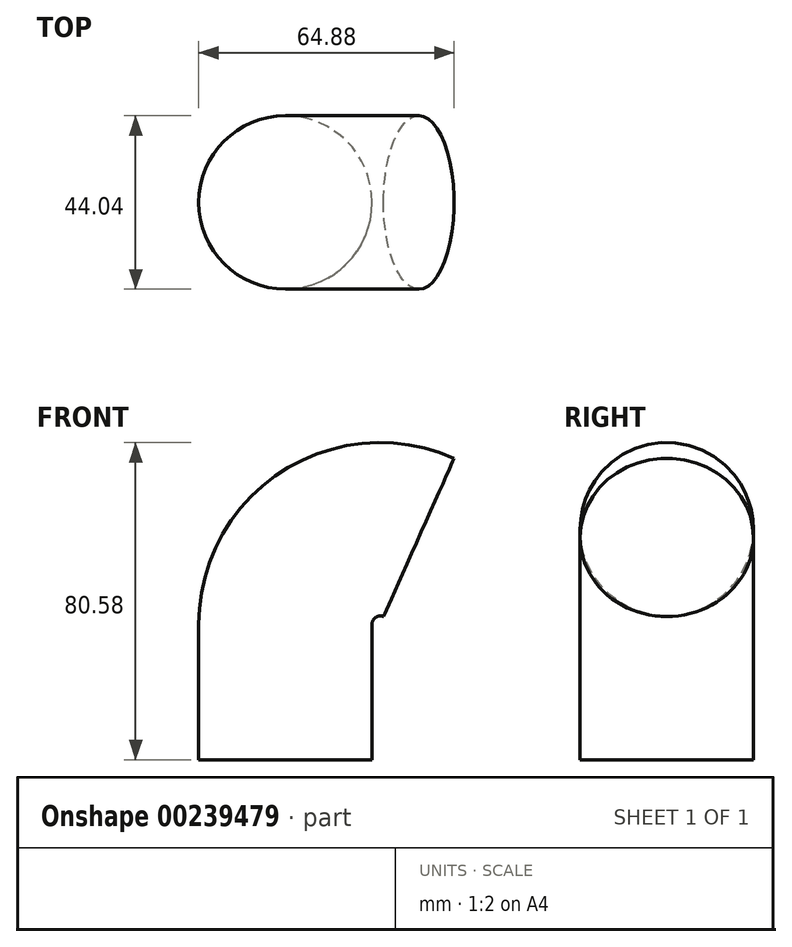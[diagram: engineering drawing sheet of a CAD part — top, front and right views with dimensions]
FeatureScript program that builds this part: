
annotation { "Feature Type Name" : "Feature", "Feature Type Description" : "" }
export const myFeature = defineFeature(function(context is Context, id is Id, definition is map)
    precondition{}
    {
        {
            var Q0;
            Q0=qCreatedBy(makeId("Front.planeOp"),FACE);
            var sketch = newSketch(context, id + "F0", { "sketchPlane" : qUnion([Q0])});
            skLineSegment(sketch, "E0", {"start": v(0, 0) * mm, "end": v(0, 34.5) * mm});
            skArc(sketch, "E1", {"start": v(33.88, 56.47) * mm, "mid": v(10.97, 54.69) * mm, "end": v(0, 34.5) * mm});
            skSolve(sketch);
        }
        {
            var Q0;
            Q0=qCreatedBy(makeId("Top.planeOp"),FACE);
            var sketch = newSketch(context, id + "F1", { "sketchPlane" : qUnion([Q0])});
            skCircle(sketch, "E2", {"center": v(0, 0) * mm, "radius": 22.02 * mm});
            skSolve(sketch);
        }
        {
            var Q0;
            Q0=makeQuery(id+"F1.imprint","IMPRINT",FACE,{"disambiguationData":[TD([[makeQuery(id+"F1.imprint","IMPRINT",EDGE,{"derivedFrom":sQuery(id+"F1.wireOp",EDGE,"E2")}),1.0]])]});
            var Q1;
            Q1 = qConstructionFilter(qBodyType(qCreatedBy(id + "F0" ,EDGE), BodyType.WIRE), ConstructionObject.NO);
            sweep(context, id + "F2", {"profiles" : qUnion([Q0]), "path" : qUnion([Q1])});
        }
    });
